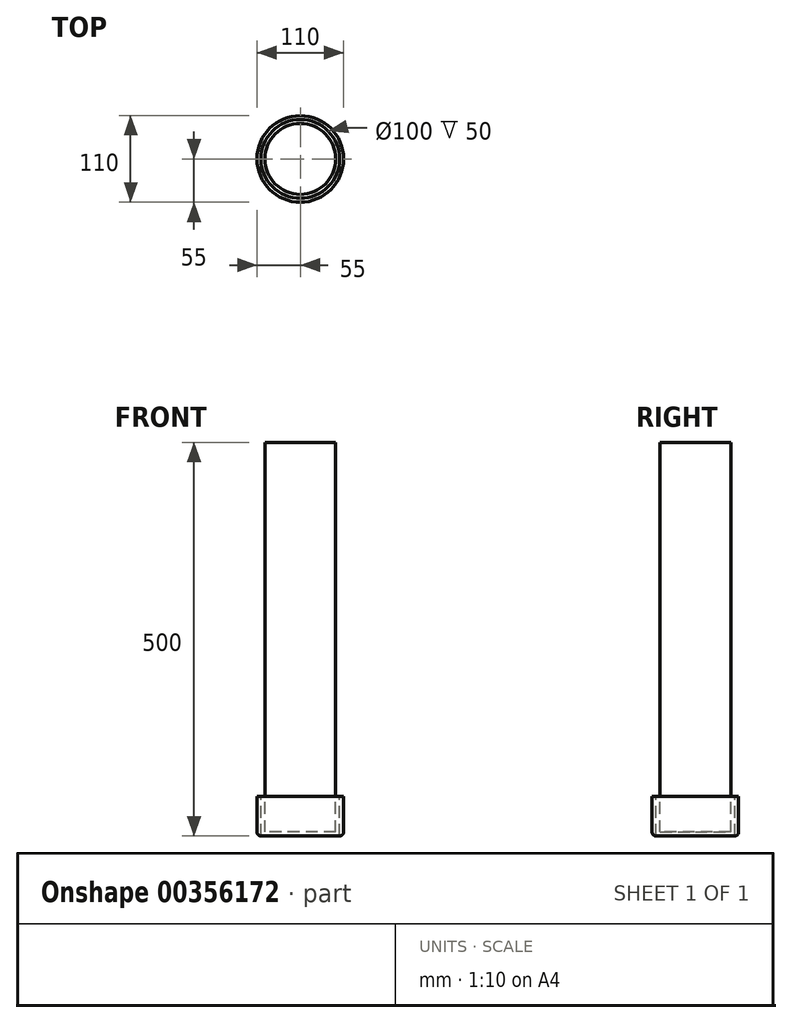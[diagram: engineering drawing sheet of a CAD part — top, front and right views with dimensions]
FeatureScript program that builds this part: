
annotation { "Feature Type Name" : "Feature", "Feature Type Description" : "" }
export const myFeature = defineFeature(function(context is Context, id is Id, definition is map)
    precondition{}
    {
        {
            var Q0;
            Q0=qCreatedBy(makeId("Front.planeOp"),FACE);
            var sketch = newSketch(context, id + "F0", { "sketchPlane" : qUnion([Q0])});
            skLineSegment(sketch, "E0.bottom", {"start": v(-50, 500) * mm, "end": v(0, 500) * mm});
            skLineSegment(sketch, "E0.top", {"start": v(-50, 0) * mm, "end": v(0, 0) * mm});
            skLineSegment(sketch, "E0.left", {"start": v(-50, 500) * mm, "end": v(-50, 0) * mm});
            skLineSegment(sketch, "E0.right", {"start": v(0, 500) * mm, "end": v(0, 0) * mm});
            skLineSegment(sketch, "E1.bottom", {"start": v(-50, 0) * mm, "end": v(-50, 0) * mm});
            skLineSegment(sketch, "E1.top", {"start": v(-50, 50) * mm, "end": v(-55, 50) * mm});
            skLineSegment(sketch, "E1.left", {"start": v(-50, 0) * mm, "end": v(-50, 50) * mm});
            skLineSegment(sketch, "E1.right", {"start": v(-55, 5) * mm, "end": v(-55, 50) * mm});
            skPoint(sketch, "E2.visualSharp", {"position": v(-55, 0) * mm});
            skArc(sketch, "E2.filletArc", {"start": v(-55, 5) * mm, "mid": v(-53.54, 1.46) * mm, "end": v(-50, 0) * mm});
            skLineSegment(sketch, "E3.bottom", {"start": v(0, 500) * mm, "end": v(-45, 500) * mm});
            skLineSegment(sketch, "E3.top", {"start": v(0, 5) * mm, "end": v(-45, 5) * mm});
            skLineSegment(sketch, "E3.left", {"start": v(0, 500) * mm, "end": v(0, 5) * mm});
            skLineSegment(sketch, "E3.right", {"start": v(-45, 500) * mm, "end": v(-45, 5) * mm});
            skSolve(sketch);
        }
        {
            var Q0;
            Q0=makeQuery(id+"F0.imprint","IMPRINT",FACE,{"disambiguationData":[TD([[makeQuery(id+"F0.imprint","IMPRINT",EDGE,{"derivedFrom":sQuery(id+"F0.wireOp",EDGE,"E1.top")}),1.0]])]});
            var Q1;
            Q1=makeQuery(id+"F0.imprint","IMPRINT",FACE,{"disambiguationData":[TD([[makeQuery(id+"F0.imprint","IMPRINT",EDGE,{"derivedFrom":sQuery(id+"F0.wireOp",EDGE,"E0.bottom")}),-1.0]])]});
            var Q2;
            Q2=sQuery(id+"F0.wireOp",EDGE,"E3.left");
            revolve(context, id + "F1", {"entities" : qUnion([Q0, Q1]), "axis" : qUnion([Q2]), "revolveType" : RevolveType.FULL});
        }
    });
